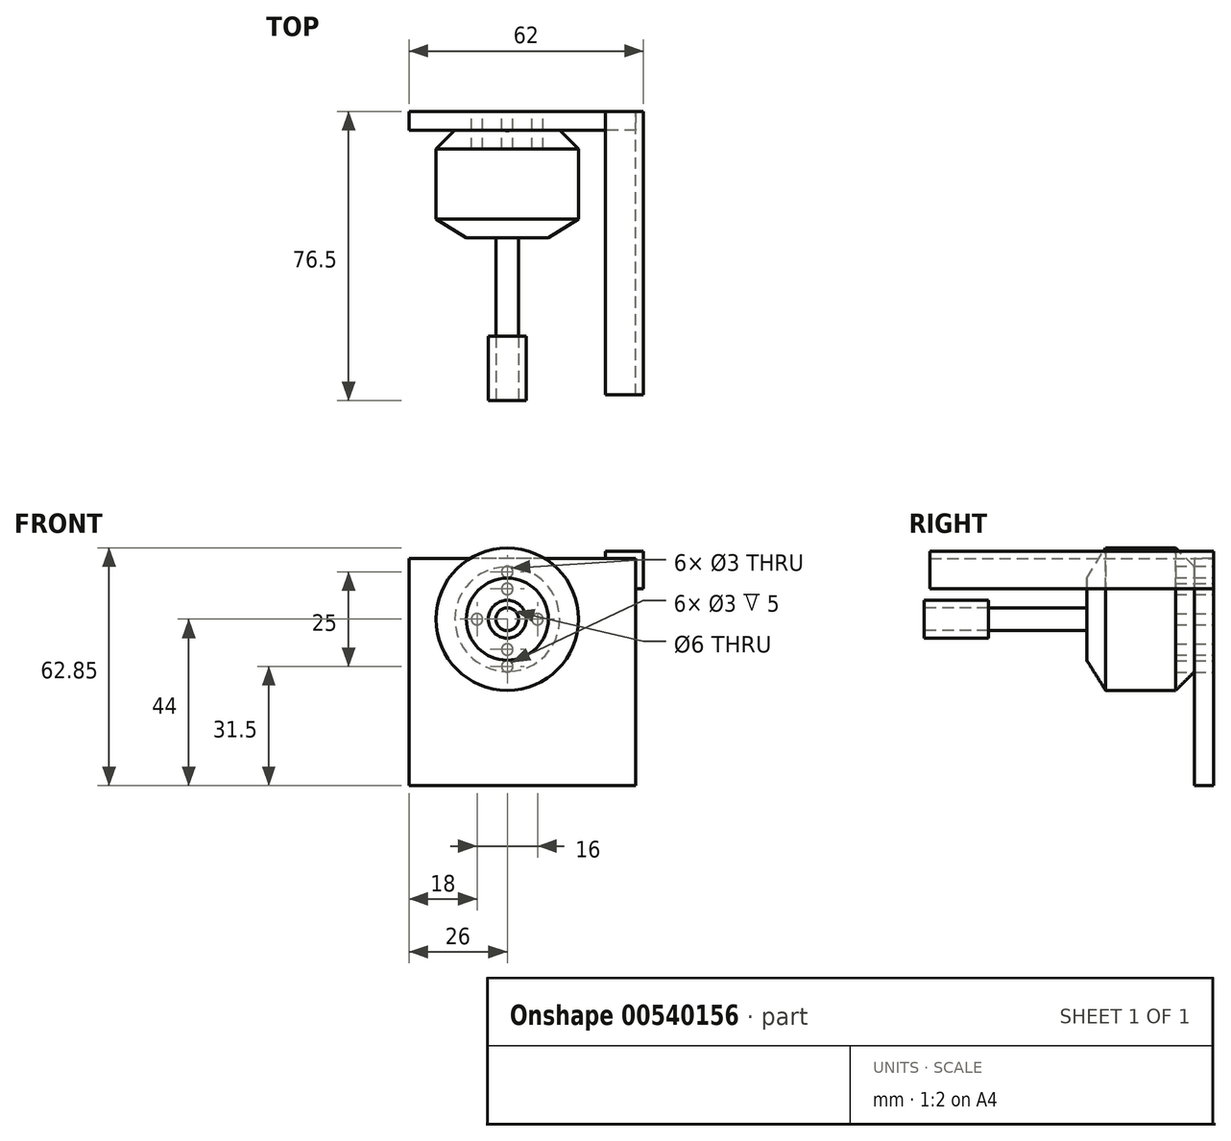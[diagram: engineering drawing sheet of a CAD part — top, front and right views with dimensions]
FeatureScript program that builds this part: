
annotation { "Feature Type Name" : "Feature", "Feature Type Description" : "" }
export const myFeature = defineFeature(function(context is Context, id is Id, definition is map)
    precondition{}
    {
        {
            var Q0;
            Q0=qCreatedBy(makeId("Front.planeOp"),FACE);
            var sketch = newSketch(context, id + "F0", { "sketchPlane" : qUnion([Q0])});
            skCircle(sketch, "E0", {"center": v(0, 0) * mm, "radius": 18.85 * mm});
            skSolve(sketch);
        }
        {
            var Q0;
            Q0 = qSketchRegion(id + "F0", true);
            extrude(context, id + "F1", {"entities" : qUnion([Q0]), "depth" : 28.5 * mm, "offsetDistance" : 25 * mm});
        }
        {
            var Q0;
            Q0=makeQuery(id+"F1.opExtrude","CAP_EDGE",EDGE,{"disambiguationData":[OSD([sQuery(id+"F0.wireOp",EDGE,"E0")])],"isStart":false});
            chamfer(context, id + "F2", {"entities" : qUnion([Q0]), "chamferType" : ChamferType.TWO_OFFSETS, "width1" : 8 * mm, "oppositeDirection" : false, "width2" : 5 * mm, "tangentPropagation" : true});
        }
        {
            var Q0;
            Q0=makeQuery(id+"F1.opExtrude","CAP_EDGE",EDGE,{"disambiguationData":[OSD([sQuery(id+"F0.wireOp",EDGE,"E0")])],"isStart":true});
            chamfer(context, id + "F3", {"entities" : qUnion([Q0]), "width" : 5 * mm, "tangentPropagation" : true});
        }
        {
            var Q0;
            Q0=makeQuery(id+"F1.opExtrude","CAP_FACE",FACE,{"disambiguationData":[OSD([sQuery(id+"F0.wireOp",EDGE,"E0")])],"isStart":false});
            var sketch = newSketch(context, id + "F4", { "sketchPlane" : qUnion([Q0])});
            skCircle(sketch, "E1", {"center": v(0, 0) * mm, "radius": 3 * mm});
            skSolve(sketch);
        }
        {
            var Q0;
            Q0 = qSketchRegion(id + "F4", true);
            extrude(context, id + "F5", {"entities" : qUnion([Q0]), "operationType" : NewBodyOperationType.ADD, "depth" : 26 * mm, "offsetDistance" : 25 * mm});
        }
        {
            var Q0;
            Q0=makeQuery(id+"F5.opExtrude","CAP_FACE",FACE,{"disambiguationData":[OSD([sQuery(id+"F4.wireOp",EDGE,"E1")])],"isStart":false});
            var sketch = newSketch(context, id + "F6", { "sketchPlane" : qUnion([Q0])});
            skCircle(sketch, "E2", {"center": v(0, 0) * mm, "radius": 5 * mm});
            skSolve(sketch);
        }
        {
            var Q0;
            Q0 = qSketchRegion(id + "F6", true);
            extrude(context, id + "F7", {"entities" : qUnion([Q0]), "depth" : 17 * mm, "offsetDistance" : 25 * mm});
        }
        {
            var Q0;
            Q0=makeQuery(id+"F7.opExtrude","CAP_FACE",FACE,{"disambiguationData":[OSD([sQuery(id+"F6.wireOp",EDGE,"E2")])],"isStart":false});
            var sketch = newSketch(context, id + "F8", { "sketchPlane" : qUnion([Q0])});
            skCircle(sketch, "E3", {"center": v(0, 0) * mm, "radius": 3 * mm});
            skSolve(sketch);
        }
        {
            var Q0;
            Q0 = qSketchRegion(id + "F8", true);
            extrude(context, id + "F9", {"entities" : qUnion([Q0]), "operationType" : NewBodyOperationType.REMOVE, "endBound" : BoundingType.UP_TO_NEXT, "oppositeDirection" : true, "depth" : 25 * mm, "offsetDistance" : 25 * mm});
        }
        {
            var Q0;
            Q0=makeQuery(id+"F1.opExtrude","CAP_FACE",FACE,{"disambiguationData":[OSD([sQuery(id+"F0.wireOp",EDGE,"E0")])],"isStart":true});
            var sketch = newSketch(context, id + "F10", { "sketchPlane" : qUnion([Q0])});
            skCircle(sketch, "E4", {"center": v(0, 0) * mm, "radius": 12.5 * mm, "construction": true});
            skCircle(sketch, "E5", {"center": v(0, 0) * mm, "radius": 8 * mm, "construction": true});
            skLineSegment(sketch, "E6", {"start": v(-13.85, 0) * mm, "end": v(13.85, 0) * mm, "construction": true});
            skLineSegment(sketch, "E7", {"start": v(0, 13.85) * mm, "end": v(0, -13.85) * mm, "construction": true});
            skCircle(sketch, "E8", {"center": v(0, 8) * mm, "radius": 1.5 * mm});
            skCircle(sketch, "E9", {"center": v(0, 12.5) * mm, "radius": 1.5 * mm});
            skCircle(sketch, "E10.MirrorC", {"center": v(0, -8) * mm, "radius": 1.5 * mm});
            skCircle(sketch, "E11.MirrorC", {"center": v(0, -12.5) * mm, "radius": 1.5 * mm});
            skCircle(sketch, "E12", {"center": v(-8, 0) * mm, "radius": 1.5 * mm});
            skCircle(sketch, "E13", {"center": v(8, 0) * mm, "radius": 1.5 * mm});
            skSolve(sketch);
        }
        {
            var Q0;
            Q0 = qSketchRegion(id + "F10", true);
            extrude(context, id + "F11", {"entities" : qUnion([Q0]), "operationType" : NewBodyOperationType.REMOVE, "oppositeDirection" : true, "depth" : 5 * mm, "offsetDistance" : 25 * mm});
        }
        {
            var Q0;
            Q0=qCreatedBy(makeId("Front.planeOp"),FACE);
            var sketch = newSketch(context, id + "F12", { "sketchPlane" : qUnion([Q0])});
            skLineSegment(sketch, "E14.bottom", {"start": v(34, 16) * mm, "end": v(-26, 16) * mm});
            skLineSegment(sketch, "E14.top", {"start": v(34, -44) * mm, "end": v(-26, -44) * mm});
            skLineSegment(sketch, "E14.left", {"start": v(34, 16) * mm, "end": v(34, -44) * mm});
            skLineSegment(sketch, "E14.right", {"start": v(-26, 16) * mm, "end": v(-26, -44) * mm});
            skSolve(sketch);
        }
        {
            var Q0;
            Q0 = qSketchRegion(id + "F12", true);
            extrude(context, id + "F13", {"entities" : qUnion([Q0]), "oppositeDirection" : true, "depth" : 5 * mm, "offsetDistance" : 25 * mm});
        }
        {
            var Q0;
            Q0=makeQuery(id+"F13.opExtrude","CAP_FACE",FACE,{"disambiguationData":[OSD([sQuery(id+"F12.wireOp",EDGE,"E14.bottom"),sQuery(id+"F12.wireOp",EDGE,"E14.top"),sQuery(id+"F12.wireOp",EDGE,"E14.left"),sQuery(id+"F12.wireOp",EDGE,"E14.right")])],"isStart":false});
            var sketch = newSketch(context, id + "F14", { "sketchPlane" : qUnion([Q0])});
            skCircle(sketch, "E15", {"center": v(0, 0) * mm, "radius": 12.5 * mm, "construction": true});
            skCircle(sketch, "E16", {"center": v(0, 0) * mm, "radius": 8 * mm, "construction": true});
            skLineSegment(sketch, "E17", {"start": v(0, 0) * mm, "end": v(0, 12.5) * mm, "construction": true});
            skLineSegment(sketch, "E18", {"start": v(0, 0) * mm, "end": v(-12.5, 0) * mm, "construction": true});
            skCircle(sketch, "E19", {"center": v(-8, 0) * mm, "radius": 1.5 * mm});
            skCircle(sketch, "E20", {"center": v(0, 8) * mm, "radius": 1.5 * mm});
            skCircle(sketch, "E21", {"center": v(0, 12.5) * mm, "radius": 1.5 * mm});
            skCircle(sketch, "E22.MirrorC", {"center": v(0, -8) * mm, "radius": 1.5 * mm});
            skCircle(sketch, "E23.MirrorC", {"center": v(0, -12.5) * mm, "radius": 1.5 * mm});
            skCircle(sketch, "E24.MirrorC", {"center": v(8, 0) * mm, "radius": 1.5 * mm});
            skSolve(sketch);
        }
        {
            var Q0;
            Q0 = qSketchRegion(id + "F14", true);
            extrude(context, id + "F15", {"entities" : qUnion([Q0]), "operationType" : NewBodyOperationType.REMOVE, "endBound" : BoundingType.UP_TO_NEXT, "oppositeDirection" : true, "depth" : 25 * mm, "offsetDistance" : 25 * mm});
        }
        {
            var Q0;
            Q0=makeQuery(id+"F13.opExtrude","CAP_FACE",FACE,{"disambiguationData":[OSD([sQuery(id+"F12.wireOp",EDGE,"E14.bottom"),sQuery(id+"F12.wireOp",EDGE,"E14.top"),sQuery(id+"F12.wireOp",EDGE,"E14.left"),sQuery(id+"F12.wireOp",EDGE,"E14.right")])],"isStart":false});
            var sketch = newSketch(context, id + "F16", { "sketchPlane" : qUnion([Q0])});
            skLineSegment(sketch, "E25", {"start": v(-34, 16) * mm, "end": v(-34, 8) * mm});
            skLineSegment(sketch, "E26", {"start": v(-34, 8) * mm, "end": v(-36, 8) * mm});
            skLineSegment(sketch, "E27", {"start": v(-36, 8) * mm, "end": v(-36, 18) * mm});
            skLineSegment(sketch, "E28", {"start": v(-36, 18) * mm, "end": v(-26, 18) * mm});
            skLineSegment(sketch, "E29", {"start": v(-26, 18) * mm, "end": v(-26, 16) * mm});
            skLineSegment(sketch, "E30", {"start": v(-26, 16) * mm, "end": v(-34, 16) * mm});
            skSolve(sketch);
        }
        {
            var Q0;
            Q0 = qSketchRegion(id + "F16", true);
            extrude(context, id + "F17", {"entities" : qUnion([Q0]), "oppositeDirection" : true, "depth" : 75 * mm, "offsetDistance" : 25 * mm});
        }
    });
